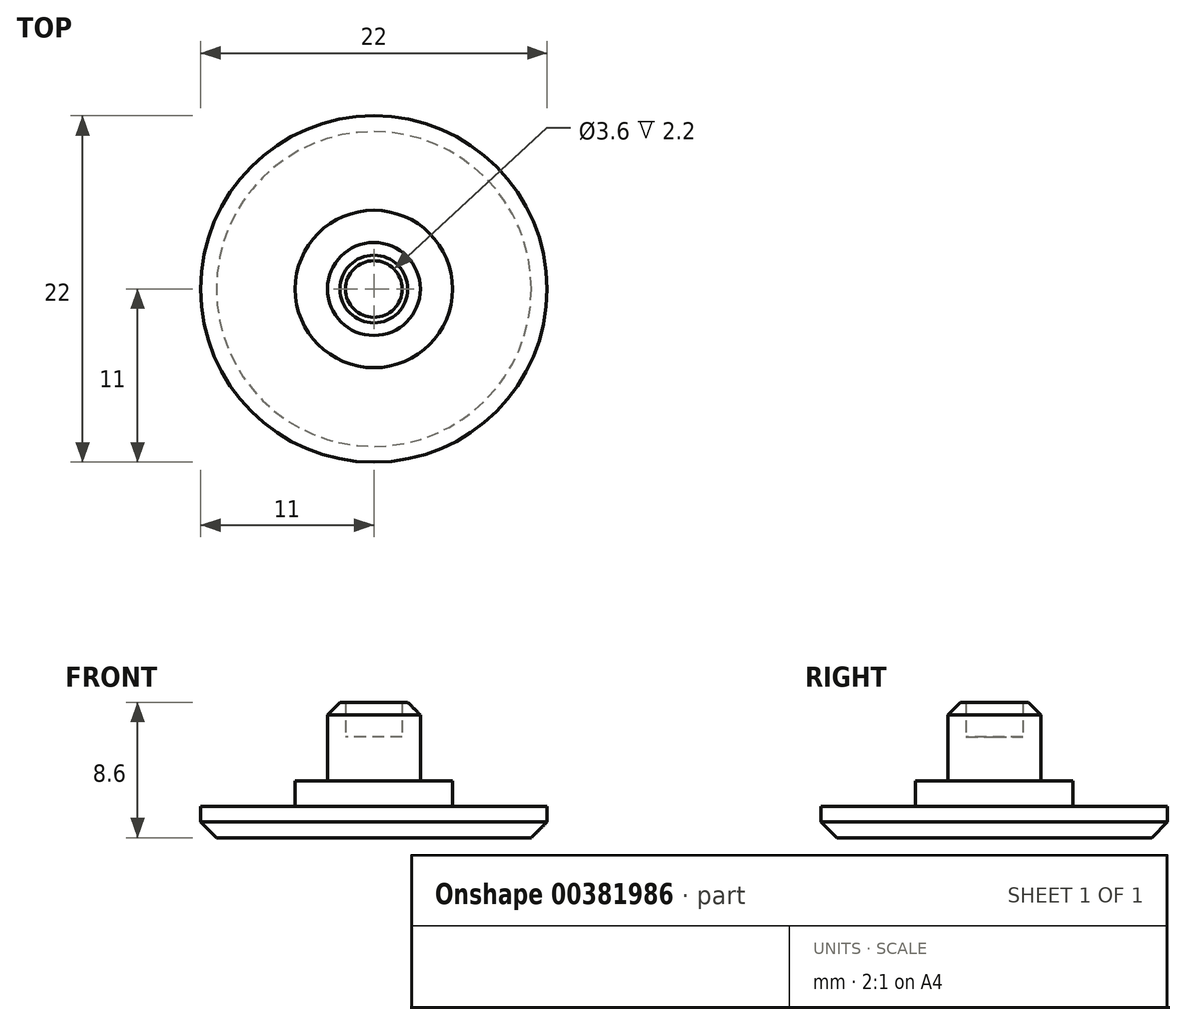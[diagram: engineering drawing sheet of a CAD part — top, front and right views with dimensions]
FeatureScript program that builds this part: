
annotation { "Feature Type Name" : "Feature", "Feature Type Description" : "" }
export const myFeature = defineFeature(function(context is Context, id is Id, definition is map)
    precondition{}
    {
        {
            var Q0;
            Q0=qCreatedBy(makeId("Top.planeOp"),FACE);
            var sketch = newSketch(context, id + "F0", { "sketchPlane" : qUnion([Q0])});
            skCircle(sketch, "E0", {"center": v(0, 0) * mm, "radius": 2.95 * mm});
            skCircle(sketch, "E1", {"center": v(0, 0) * mm, "radius": 11 * mm});
            skCircle(sketch, "E2", {"center": v(0, 0) * mm, "radius": 5 * mm});
            skCircle(sketch, "E3", {"center": v(0, 0) * mm, "radius": 1.8 * mm});
            skSolve(sketch);
        }
        {
            var Q0;
            Q0=makeQuery(id+"F0.imprint","IMPRINT",FACE,{"disambiguationData":[TD([[makeQuery(id+"F0.imprint","IMPRINT",EDGE,{"derivedFrom":sQuery(id+"F0.wireOp",EDGE,"E1")}),1.0]])]});
            extrude(context, id + "F1", {"entities" : qUnion([Q0]), "depth" : 2 * mm, "offsetDistance" : 25 * mm});
        }
        {
            var Q0;
            Q0=makeQuery(id+"F0.imprint","IMPRINT",FACE,{"disambiguationData":[TD([[makeQuery(id+"F0.imprint","IMPRINT",EDGE,{"derivedFrom":sQuery(id+"F0.wireOp",EDGE,"E0")}),-1.0]])]});
            extrude(context, id + "F2", {"entities" : qUnion([Q0]), "operationType" : NewBodyOperationType.ADD, "depth" : 3.6 * mm, "offsetDistance" : 25 * mm});
        }
        {
            var Q0;
            Q0=makeQuery(id+"F0.imprint","IMPRINT",FACE,{"disambiguationData":[TD([[makeQuery(id+"F0.imprint","IMPRINT",EDGE,{"derivedFrom":sQuery(id+"F0.wireOp",EDGE,"E0")}),1.0]])]});
            var Q1;
            Q1=makeQuery(id+"F0.imprint","IMPRINT",FACE,{"disambiguationData":[TD([[makeQuery(id+"F0.imprint","IMPRINT",EDGE,{"derivedFrom":sQuery(id+"F0.wireOp",EDGE,"E3")}),1.0]])]});
            extrude(context, id + "F3", {"entities" : qUnion([Q0, Q1]), "operationType" : NewBodyOperationType.ADD, "depth" : (3.6 + 2.8) * mm, "offsetDistance" : 25 * mm});
        }
        {
            var Q0;
            Q0=makeQuery(id+"F0.imprint","IMPRINT",FACE,{"disambiguationData":[TD([[makeQuery(id+"F0.imprint","IMPRINT",EDGE,{"derivedFrom":sQuery(id+"F0.wireOp",EDGE,"E0")}),-1.0]])]});
            var Q1;
            Q1=makeQuery(id+"F0.imprint","IMPRINT",FACE,{"disambiguationData":[TD([[makeQuery(id+"F0.imprint","IMPRINT",EDGE,{"derivedFrom":sQuery(id+"F0.wireOp",EDGE,"E0")}),1.0]])]});
            var Q2;
            Q2=makeQuery(id+"F0.imprint","IMPRINT",FACE,{"disambiguationData":[TD([[makeQuery(id+"F0.imprint","IMPRINT",EDGE,{"derivedFrom":sQuery(id+"F0.wireOp",EDGE,"E3")}),1.0]])]});
            extrude(context, id + "F4", {"entities" : qUnion([Q0, Q1, Q2]), "operationType" : NewBodyOperationType.REMOVE, "depth" : 1 * mm, "offsetDistance" : 25 * mm});
        }
        {
            var Q0;
            Q0=makeQuery(id+"F1.opExtrude","CAP_EDGE",EDGE,{"disambiguationData":[OSD([sQuery(id+"F0.wireOp",EDGE,"E1")])],"isStart":true});
            chamfer(context, id + "F5", {"entities" : qUnion([Q0]), "width" : 1 * mm, "tangentPropagation" : true});
        }
        {
            var Q0;
            Q0=makeQuery(id+"F4.boolean.opBoolean","COPY",EDGE,{"derivedFrom":makeQuery(id+"F4.opExtrude","CAP_EDGE",EDGE,{"disambiguationData":[OSD([sQuery(id+"F0.wireOp",EDGE,"E2")])],"isStart":false})});
            fillet(context, id + "F6", {"entities" : qUnion([Q0]), "radius" : 10 * mm, "tangentPropagation" : true, "allowEdgeOverflow" : false});
        }
        {
            var Q0;
            Q0=makeQuery(id+"F0.imprint","IMPRINT",FACE,{"disambiguationData":[TD([[makeQuery(id+"F0.imprint","IMPRINT",EDGE,{"derivedFrom":sQuery(id+"F0.wireOp",EDGE,"E1")}),1.0]])]});
            extrude(context, id + "F7", {"entities" : qUnion([Q0]), "depth" : 2 * mm, "offsetDistance" : 25 * mm});
        }
        {
            var Q0;
            Q0=makeQuery(id+"F0.imprint","IMPRINT",FACE,{"disambiguationData":[TD([[makeQuery(id+"F0.imprint","IMPRINT",EDGE,{"derivedFrom":sQuery(id+"F0.wireOp",EDGE,"E0")}),-1.0]])]});
            extrude(context, id + "F8", {"entities" : qUnion([Q0]), "operationType" : NewBodyOperationType.ADD, "depth" : 2.6 * mm, "offsetDistance" : 25 * mm});
        }
        {
            var Q0;
            Q0=makeQuery(id+"F0.imprint","IMPRINT",FACE,{"disambiguationData":[TD([[makeQuery(id+"F0.imprint","IMPRINT",EDGE,{"derivedFrom":sQuery(id+"F0.wireOp",EDGE,"E0")}),1.0]])]});
            extrude(context, id + "F9", {"entities" : qUnion([Q0]), "operationType" : NewBodyOperationType.ADD, "depth" : (6 + 2.6) * mm, "offsetDistance" : 25 * mm});
        }
        {
            var Q0;
            Q0=makeQuery(id+"F7.opExtrude","CAP_EDGE",EDGE,{"disambiguationData":[OSD([sQuery(id+"F0.wireOp",EDGE,"E1")])],"isStart":true});
            chamfer(context, id + "F10", {"entities" : qUnion([Q0]), "width" : 1 * mm, "tangentPropagation" : true});
        }
        {
            var Q0;
            Q0=makeQuery(id+"F9.opExtrude","CAP_EDGE",EDGE,{"disambiguationData":[OSD([sQuery(id+"F0.wireOp",EDGE,"E0")])],"isStart":false});
            chamfer(context, id + "F11", {"entities" : qUnion([Q0]), "width" : .8 * mm, "tangentPropagation" : true});
        }
        {
            var Q0;
            Q0=makeQuery(id+"F0.imprint","IMPRINT",FACE,{"disambiguationData":[TD([[makeQuery(id+"F0.imprint","IMPRINT",EDGE,{"derivedFrom":sQuery(id+"F0.wireOp",EDGE,"E3")}),1.0]])]});
            extrude(context, id + "F12", {"entities" : qUnion([Q0]), "operationType" : NewBodyOperationType.ADD, "depth" : 2 * mm, "offsetDistance" : 25 * mm});
        }
    });
